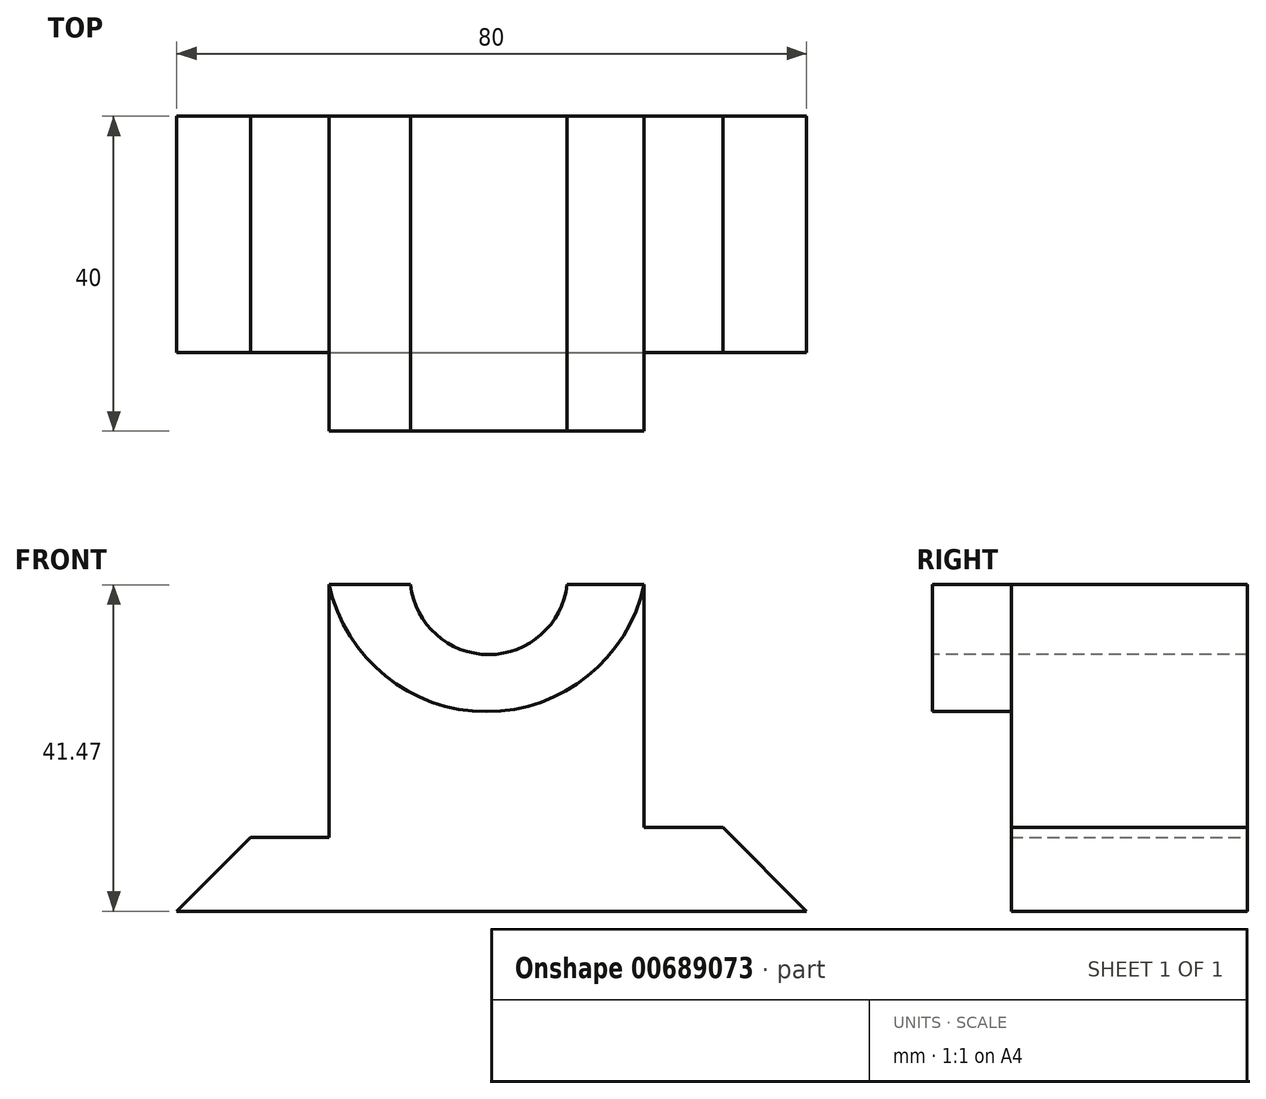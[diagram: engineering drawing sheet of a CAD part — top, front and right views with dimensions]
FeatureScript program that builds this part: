
annotation { "Feature Type Name" : "Feature", "Feature Type Description" : "" }
export const myFeature = defineFeature(function(context is Context, id is Id, definition is map)
    precondition{}
    {
        {
            var Q0;
            Q0=qCreatedBy(makeId("Front.planeOp"),FACE);
            var sketch = newSketch(context, id + "F0", { "sketchPlane" : qUnion([Q0])});
            skLineSegment(sketch, "E0", {"start": v(0, 0) * mm, "end": v(80, 0) * mm});
            skLineSegment(sketch, "E1", {"start": v(80, 0) * mm, "end": v(69.36, 10.64) * mm});
            skLineSegment(sketch, "E2", {"start": v(69.36, 10.64) * mm, "end": v(59.36, 10.64) * mm});
            skLineSegment(sketch, "E3", {"start": v(59.36, 10.64) * mm, "end": v(59.36, 41.47) * mm});
            skLineSegment(sketch, "E4", {"start": v(59.36, 41.47) * mm, "end": v(19.36, 41.47) * mm});
            skLineSegment(sketch, "E5", {"start": v(19.36, 41.47) * mm, "end": v(19.36, 9.36) * mm});
            skLineSegment(sketch, "E6", {"start": v(19.36, 9.36) * mm, "end": v(9.36, 9.36) * mm});
            skLineSegment(sketch, "E7", {"start": v(9.36, 9.36) * mm, "end": v(0, 0) * mm});
            skSolve(sketch);
        }
        {
            var Q0;
            Q0=makeQuery(id+"F0.imprint","IMPRINT",FACE,{"disambiguationData":[TD([[makeQuery(id+"F0.imprint","IMPRINT",EDGE,{"derivedFrom":sQuery(id+"F0.wireOp",EDGE,"E0")}),1.0]])]});
            extrude(context, id + "F1", {"entities" : qUnion([Q0]), "depth" : 30 * mm, "offsetDistance" : 25 * mm});
        }
        {
            var Q0;
            Q0=makeQuery(id+"F1.opExtrude","CAP_FACE",FACE,{"disambiguationData":[OSD([sQuery(id+"F0.wireOp",EDGE,"E0"),sQuery(id+"F0.wireOp",EDGE,"E1"),sQuery(id+"F0.wireOp",EDGE,"E2"),sQuery(id+"F0.wireOp",EDGE,"E3"),sQuery(id+"F0.wireOp",EDGE,"E4"),sQuery(id+"F0.wireOp",EDGE,"E5"),sQuery(id+"F0.wireOp",EDGE,"E6"),sQuery(id+"F0.wireOp",EDGE,"E7")])],"isStart":false});
            var sketch = newSketch(context, id + "F2", { "sketchPlane" : qUnion([Q0])});
            skArc(sketch, "E8", {"start": v(19.36, 41.47) * mm, "mid": v(39.36, 25.34) * mm, "end": v(59.36, 41.47) * mm});
            skLineSegment(sketch, "E9", {"start": v(19.36, 41.47) * mm, "end": v(59.36, 41.47) * mm});
            skSolve(sketch);
        }
        {
            var Q0;
            Q0=makeQuery(id+"F2.imprint","IMPRINT",FACE,{"disambiguationData":[TD([[makeQuery(id+"F2.imprint","IMPRINT",EDGE,{"derivedFrom":sQuery(id+"F2.wireOp",EDGE,"E8")}),1.0]])]});
            extrude(context, id + "F3", {"entities" : qUnion([Q0]), "operationType" : NewBodyOperationType.ADD, "depth" : 10 * mm, "offsetDistance" : 25 * mm});
        }
        {
            var Q0;
            Q0=makeQuery(id+"F3.opExtrude","CAP_FACE",FACE,{"disambiguationData":[OSD([sQuery(id+"F2.wireOp",EDGE,"E8"),sQuery(id+"F2.wireOp",EDGE,"E9")])],"isStart":false});
            var sketch = newSketch(context, id + "F4", { "sketchPlane" : qUnion([Q0])});
            skArc(sketch, "E10", {"start": v(29.7, 41.47) * mm, "mid": v(39.63, 32.6) * mm, "end": v(49.57, 41.47) * mm});
            skSolve(sketch);
        }
        {
            var Q0;
            {var subQ0=sQuery(id+"F4.wireOp",EDGE,"E10");Q0=makeQuery(id+"F4.imprint","IMPRINT",FACE,{"disambiguationData":[TD([[makeQuery(id+"F4.imprint","IMPRINT",EDGE,{"derivedFrom":subQ0}),1.0]])]});}
            extrude(context, id + "F5", {"entities" : qUnion([Q0]), "operationType" : NewBodyOperationType.REMOVE, "endBound" : BoundingType.THROUGH_ALL, "oppositeDirection" : true, "depth" : 25 * mm, "offsetDistance" : 25 * mm});
        }
    });
